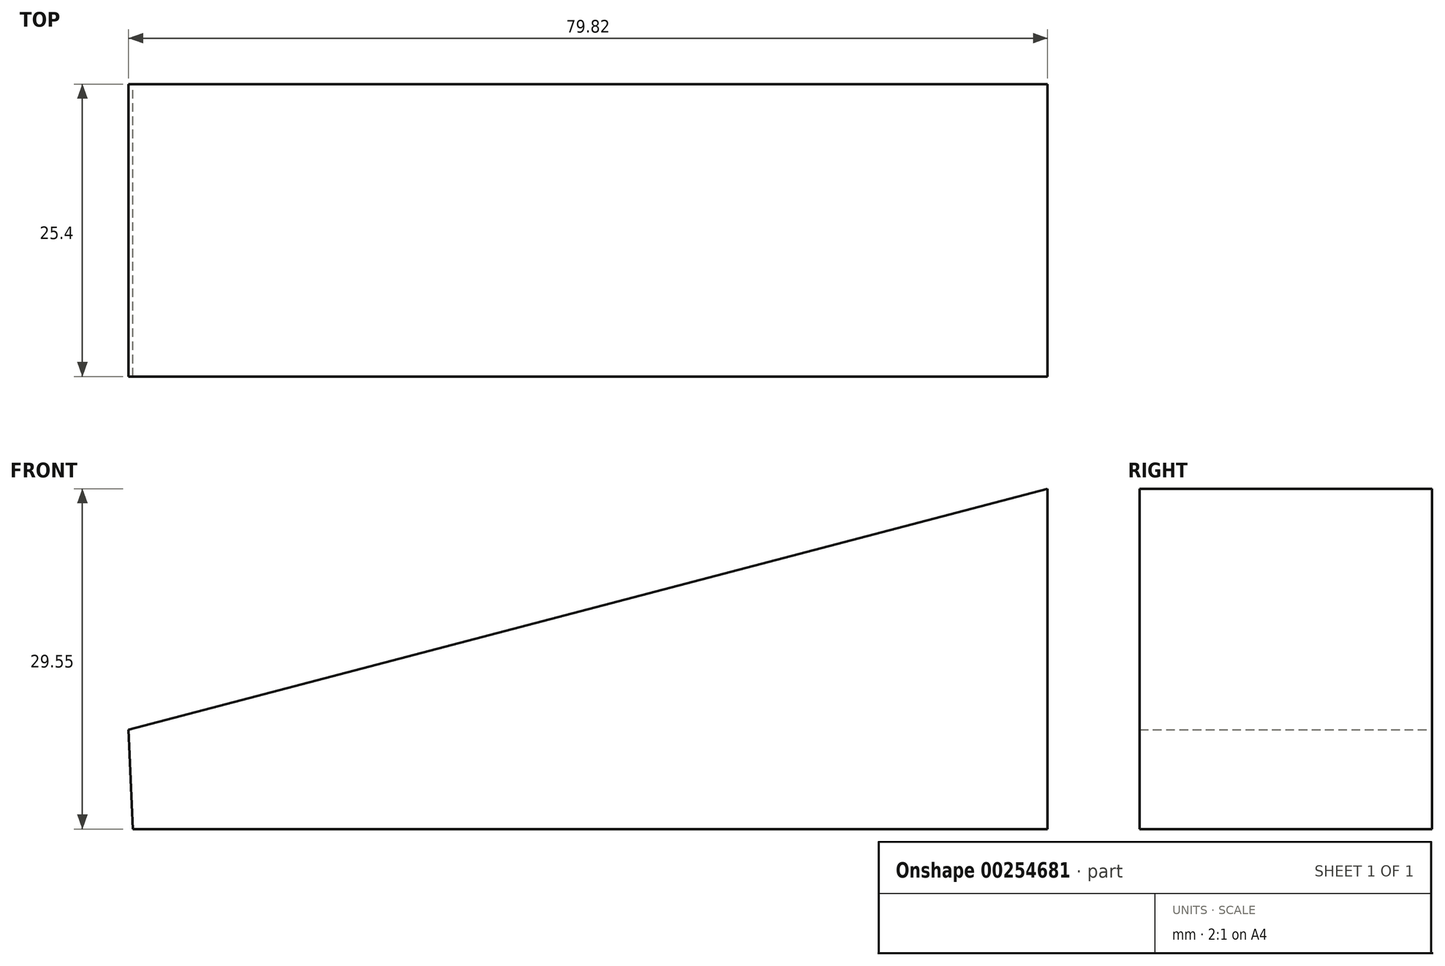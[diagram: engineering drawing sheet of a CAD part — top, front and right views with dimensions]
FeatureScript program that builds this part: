
annotation { "Feature Type Name" : "Feature", "Feature Type Description" : "" }
export const myFeature = defineFeature(function(context is Context, id is Id, definition is map)
    precondition{}
    {
        {
            var Q0;
            Q0=qCreatedBy(makeId("Front.planeOp"),FACE);
            var sketch = newSketch(context, id + "F0", { "sketchPlane" : qUnion([Q0])});
            skLineSegment(sketch, "E0", {"start": v(-38.57, 0) * mm, "end": v(40.87, 0) * mm});
            skLineSegment(sketch, "E1", {"start": v(40.87, 0) * mm, "end": v(40.87, 29.55) * mm});
            skLineSegment(sketch, "E2", {"start": v(40.87, 29.55) * mm, "end": v(-38.95, 8.63) * mm});
            skLineSegment(sketch, "E3", {"start": v(-38.95, 8.63) * mm, "end": v(-38.57, 0) * mm});
            skSolve(sketch);
        }
        {
            var Q0;
            Q0=makeQuery(id+"F0.imprint","IMPRINT",FACE,{"disambiguationData":[TD([[makeQuery(id+"F0.imprint","IMPRINT",EDGE,{"derivedFrom":sQuery(id+"F0.wireOp",EDGE,"E0")}),1.0]])]});
            extrude(context, id + "F1", {"entities" : qUnion([Q0]), "depth" : 25.4 * mm});
        }
        {
            var Q0;
            Q0=makeQuery(id+"F1.opExtrude","CAP_FACE",FACE,{"disambiguationData":[OSD([sQuery(id+"F0.wireOp",EDGE,"E0"),sQuery(id+"F0.wireOp",EDGE,"E1"),sQuery(id+"F0.wireOp",EDGE,"E2"),sQuery(id+"F0.wireOp",EDGE,"E3")])],"isStart":false});
            var sketch = newSketch(context, id + "F2", { "sketchPlane" : qUnion([Q0])});
            skCircle(sketch, "E4", {"center": v(-30.76, 2.48) * mm, "radius": 1.43 * mm});
            skSolve(sketch);
        }
        {
            var Q0;
            Q0=makeQuery(id+"F2.imprint","IMPRINT",FACE,{"disambiguationData":[TD([[makeQuery(id+"F2.imprint","IMPRINT",EDGE,{"derivedFrom":sQuery(id+"F2.wireOp",EDGE,"E4")}),-1.0]])]});
            var sketch = newSketch(context, id + "F3", { "sketchPlane" : qUnion([Q0])});
            skCircle(sketch, "E5", {"center": v(32.18, 2.3) * mm, "radius": 1.47 * mm});
            skSolve(sketch);
        }
        {
            var Q0;
            Q0=sQuery(id+"F2.wireOp",EDGE,"E4");
            var Q1;
            Q1=sQuery(id+"F3.wireOp",EDGE,"E5");
            extrude(context, id + "F4", {"bodyType" : ToolBodyType.SURFACE, "surfaceEntities" : qUnion([Q0, Q1]), "depth" : 50.8 * mm});
        }
    });
